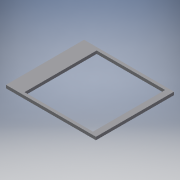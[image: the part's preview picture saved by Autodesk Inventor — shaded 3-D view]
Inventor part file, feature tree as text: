
AUTODESK INVENTOR PART (.ipt)
format: ipt  version: 2018.3 (Build 223284000, 284)  size: 113,152 bytes
history: native  units: mm
features: extrude x4, sketch x4
ambient origin geometry x8: Origin, YZ Plane, XZ Plane, XY Plane, X Axis, Y Axis, Z Axis, Center Point
bodies: Solid1 (feature_tree)
feature tree (8):
  extrude  "Extrusion1"  Depth=52.5mm
  extrude  "Extrusion2"  Depth=46.0mm
  extrude  "Extrusion3"  Depth=48.5mm TaperAngle=0.0deg
  extrude  "Extrusion4"  Depth=2.0mm TaperAngle=0.0deg
  sketch  "Sketch1"  dims[d0=50.0mm d1=52.5mm]
  sketch  "Sketch2"  dims[d2=2.0mm d3=0.0mm d4=46.0mm]
  sketch  "Sketch3"  dims[d5=48.5mm d6=10.0mm d7=0.0mm]
  sketch  "Sketch4"  dims[d8=8.5mm d9=0.0mm d10=2.0mm d11=0.0mm]
